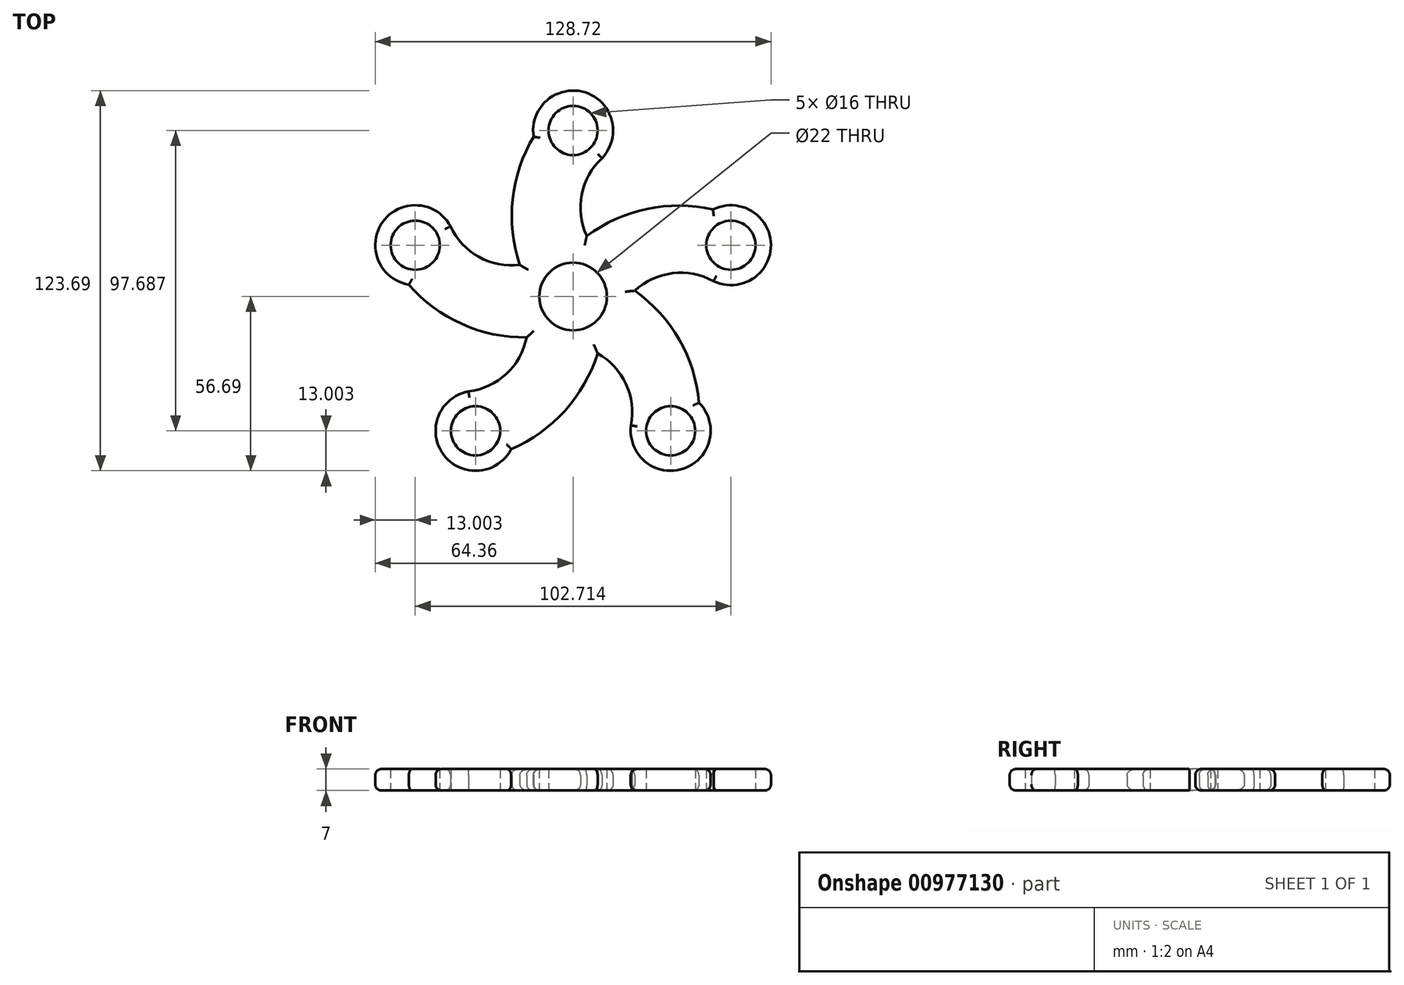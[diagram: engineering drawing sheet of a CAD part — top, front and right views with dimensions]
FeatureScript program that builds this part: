
annotation { "Feature Type Name" : "Feature", "Feature Type Description" : "" }
export const myFeature = defineFeature(function(context is Context, id is Id, definition is map)
    precondition{}
    {
        {
            var Q0;
            Q0=qCreatedBy(makeId("Top.planeOp"),FACE);
            var sketch = newSketch(context, id + "F0", { "sketchPlane" : qUnion([Q0])});
            skCircle(sketch, "E0", {"center": v(0, 0) * mm, "radius": 11 * mm});
            skCircle(sketch, "E1", {"center": v(0, 0) * mm, "radius": 16 * mm});
            skCircle(sketch, "E2", {"center": v(0, 54) * mm, "radius": 8 * mm});
            skCircle(sketch, "E3", {"center": v(0, 54) * mm, "radius": 13 * mm});
            skArc(sketch, "E4", {"start": v(9.38, 45) * mm, "mid": v(2.44, 27.47) * mm, "end": v(11.62, 11) * mm});
            skArc(sketch, "E5", {"start": v(-12.85, 52) * mm, "mid": v(-19.9, 28.8) * mm, "end": v(-15.2, 5) * mm});
            skSolve(sketch);
        }
        {
            var Q0;
            Q0=makeQuery(id+"F0.imprint","IMPRINT",FACE,{"disambiguationData":[TD([[makeQuery(id+"F0.imprint","IMPRINT",EDGE,{"derivedFrom":sQuery(id+"F0.wireOp",EDGE,"E0")}),-1.0]])]});
            var Q1;
            {var subQ0=sQuery(id+"F0.wireOp",EDGE,"E5");Q1=makeQuery(id+"F0.imprint","IMPRINT",FACE,{"disambiguationData":[TD([[makeQuery(id+"F0.imprint","IMPRINT",EDGE,{"derivedFrom":subQ0}),1.0]])]});}
            var Q2;
            Q2=makeQuery(id+"F0.imprint","IMPRINT",FACE,{"disambiguationData":[TD([[makeQuery(id+"F0.imprint","IMPRINT",EDGE,{"derivedFrom":sQuery(id+"F0.wireOp",EDGE,"E2")}),-1.0]])]});
            extrude(context, id + "F1", {"entities" : qUnion([Q0, Q1, Q2]), "depth" : 7 * mm, "offsetDistance" : 25 * mm});
        }
        {
            var Q0;
            Q0=makeQuery(id+"F1.opExtrude","SWEPT_BODY",BODY,{"disambiguationData":[OSD([sQuery(id+"F0.wireOp",EDGE,"E0"),sQuery(id+"F0.wireOp",EDGE,"E1"),sQuery(id+"F0.wireOp",EDGE,"E2"),sQuery(id+"F0.wireOp",EDGE,"E3"),sQuery(id+"F0.wireOp",EDGE,"E4"),sQuery(id+"F0.wireOp",EDGE,"E5")])]});
            var Q1;
            Q1=sQuery(id+"F0.wireOp",EDGE,"E0");
            circularPattern(context, id + "F2", {"operationType" : NewBodyOperationType.ADD, "entities" : qUnion([Q0]), "axis" : qUnion([Q1]), "angle" : 360 * degree, "instanceCount" : 5, "equalSpace" : true});
        }
        {
            var Q0;
            Q0=makeQuery(id+"F2.opPattern","COPY",EDGE,{"derivedFrom":makeQuery(id+"F1.opExtrude","CAP_EDGE",EDGE,{"disambiguationData":[OSD([sQuery(id+"F0.wireOp",EDGE,"E4")])],"isStart":true}),"instanceName":"3"});
            var Q1;
            Q1=makeQuery(id+"F2.opPattern","COPY",EDGE,{"derivedFrom":makeQuery(id+"F1.opExtrude","CAP_EDGE",EDGE,{"disambiguationData":[OSD([sQuery(id+"F0.wireOp",EDGE,"E3")])],"isStart":true}),"instanceName":"3"});
            var Q2;
            Q2=makeQuery(id+"F2.opPattern","COPY",EDGE,{"derivedFrom":makeQuery(id+"F1.opExtrude","CAP_EDGE",EDGE,{"disambiguationData":[OSD([sQuery(id+"F0.wireOp",EDGE,"E4")])],"isStart":false}),"instanceName":"3"});
            var Q3;
            Q3=makeQuery(id+"F2.opPattern","COPY",EDGE,{"derivedFrom":makeQuery(id+"F1.opExtrude","CAP_EDGE",EDGE,{"disambiguationData":[OSD([sQuery(id+"F0.wireOp",EDGE,"E3")])],"isStart":false}),"instanceName":"3"});
            var Q4;
            Q4=makeQuery(id+"F2.opPattern","COPY",EDGE,{"derivedFrom":makeQuery(id+"F1.opExtrude","CAP_EDGE",EDGE,{"disambiguationData":[OSD([sQuery(id+"F0.wireOp",EDGE,"E5")])],"isStart":true}),"instanceName":"2"});
            var Q5;
            Q5=makeQuery(id+"F2.opPattern","COPY",EDGE,{"derivedFrom":makeQuery(id+"F1.opExtrude","CAP_EDGE",EDGE,{"disambiguationData":[OSD([sQuery(id+"F0.wireOp",EDGE,"E5")])],"isStart":false}),"instanceName":"2"});
            var Q6;
            Q6=makeQuery(id+"F2.opPattern","COPY",EDGE,{"derivedFrom":makeQuery(id+"F1.opExtrude","CAP_EDGE",EDGE,{"disambiguationData":[OSD([sQuery(id+"F0.wireOp",EDGE,"E3")])],"isStart":true}),"instanceName":"2"});
            var Q7;
            Q7=makeQuery(id+"F2.opPattern","COPY",EDGE,{"derivedFrom":makeQuery(id+"F1.opExtrude","CAP_EDGE",EDGE,{"disambiguationData":[OSD([sQuery(id+"F0.wireOp",EDGE,"E4")])],"isStart":true}),"instanceName":"2"});
            var Q8;
            Q8=makeQuery(id+"F2.opPattern","COPY",EDGE,{"derivedFrom":makeQuery(id+"F1.opExtrude","CAP_EDGE",EDGE,{"disambiguationData":[OSD([sQuery(id+"F0.wireOp",EDGE,"E5")])],"isStart":false}),"instanceName":"3"});
            var Q9;
            Q9=makeQuery(id+"F2.opPattern","COPY",EDGE,{"derivedFrom":makeQuery(id+"F1.opExtrude","CAP_EDGE",EDGE,{"disambiguationData":[OSD([sQuery(id+"F0.wireOp",EDGE,"E5")])],"isStart":true}),"instanceName":"3"});
            var Q10;
            Q10=makeQuery(id+"F2.opPattern","COPY",EDGE,{"derivedFrom":makeQuery(id+"F1.opExtrude","CAP_EDGE",EDGE,{"disambiguationData":[OSD([sQuery(id+"F0.wireOp",EDGE,"E4")])],"isStart":true}),"instanceName":"4"});
            var Q11;
            Q11=makeQuery(id+"F2.opPattern","COPY",EDGE,{"derivedFrom":makeQuery(id+"F1.opExtrude","CAP_EDGE",EDGE,{"disambiguationData":[OSD([sQuery(id+"F0.wireOp",EDGE,"E4")])],"isStart":false}),"instanceName":"4"});
            var Q12;
            Q12=makeQuery(id+"F2.opPattern","COPY",EDGE,{"derivedFrom":makeQuery(id+"F1.opExtrude","CAP_EDGE",EDGE,{"disambiguationData":[OSD([sQuery(id+"F0.wireOp",EDGE,"E3")])],"isStart":true}),"instanceName":"4"});
            var Q13;
            Q13=makeQuery(id+"F2.opPattern","COPY",EDGE,{"derivedFrom":makeQuery(id+"F1.opExtrude","CAP_EDGE",EDGE,{"disambiguationData":[OSD([sQuery(id+"F0.wireOp",EDGE,"E3")])],"isStart":false}),"instanceName":"4"});
            var Q14;
            Q14=makeQuery(id+"F2.opPattern","COPY",EDGE,{"derivedFrom":makeQuery(id+"F1.opExtrude","CAP_EDGE",EDGE,{"disambiguationData":[OSD([sQuery(id+"F0.wireOp",EDGE,"E5")])],"isStart":true}),"instanceName":"4"});
            var Q15;
            Q15=makeQuery(id+"F2.opPattern","COPY",EDGE,{"derivedFrom":makeQuery(id+"F1.opExtrude","CAP_EDGE",EDGE,{"disambiguationData":[OSD([sQuery(id+"F0.wireOp",EDGE,"E5")])],"isStart":false}),"instanceName":"4"});
            var Q16;
            Q16=makeQuery(id+"F1.opExtrude","CAP_EDGE",EDGE,{"disambiguationData":[OSD([sQuery(id+"F0.wireOp",EDGE,"E4")])],"isStart":true});
            var Q17;
            Q17=makeQuery(id+"F1.opExtrude","CAP_EDGE",EDGE,{"disambiguationData":[OSD([sQuery(id+"F0.wireOp",EDGE,"E4")])],"isStart":false});
            var Q18;
            Q18=makeQuery(id+"F1.opExtrude","CAP_EDGE",EDGE,{"disambiguationData":[OSD([sQuery(id+"F0.wireOp",EDGE,"E5")])],"isStart":false});
            var Q19;
            Q19=makeQuery(id+"F2.opPattern","COPY",EDGE,{"derivedFrom":makeQuery(id+"F1.opExtrude","CAP_EDGE",EDGE,{"disambiguationData":[OSD([sQuery(id+"F0.wireOp",EDGE,"E4")])],"isStart":true}),"instanceName":"1"});
            var Q20;
            Q20=makeQuery(id+"F2.opPattern","COPY",EDGE,{"derivedFrom":makeQuery(id+"F1.opExtrude","CAP_EDGE",EDGE,{"disambiguationData":[OSD([sQuery(id+"F0.wireOp",EDGE,"E4")])],"isStart":false}),"instanceName":"1"});
            var Q21;
            Q21=makeQuery(id+"F2.opPattern","COPY",EDGE,{"derivedFrom":makeQuery(id+"F1.opExtrude","CAP_EDGE",EDGE,{"disambiguationData":[OSD([sQuery(id+"F0.wireOp",EDGE,"E3")])],"isStart":true}),"instanceName":"1"});
            var Q22;
            Q22=makeQuery(id+"F2.opPattern","COPY",EDGE,{"derivedFrom":makeQuery(id+"F1.opExtrude","CAP_EDGE",EDGE,{"disambiguationData":[OSD([sQuery(id+"F0.wireOp",EDGE,"E3")])],"isStart":false}),"instanceName":"1"});
            var Q23;
            Q23=makeQuery(id+"F2.opPattern","COPY",EDGE,{"derivedFrom":makeQuery(id+"F1.opExtrude","CAP_EDGE",EDGE,{"disambiguationData":[OSD([sQuery(id+"F0.wireOp",EDGE,"E5")])],"isStart":true}),"instanceName":"1"});
            var Q24;
            Q24=makeQuery(id+"F2.opPattern","COPY",EDGE,{"derivedFrom":makeQuery(id+"F1.opExtrude","CAP_EDGE",EDGE,{"disambiguationData":[OSD([sQuery(id+"F0.wireOp",EDGE,"E5")])],"isStart":false}),"instanceName":"1"});
            var Q25;
            Q25=makeQuery(id+"F2.opPattern","COPY",EDGE,{"derivedFrom":makeQuery(id+"F1.opExtrude","CAP_EDGE",EDGE,{"disambiguationData":[OSD([sQuery(id+"F0.wireOp",EDGE,"E3")])],"isStart":false}),"instanceName":"2"});
            var Q26;
            Q26=makeQuery(id+"F1.opExtrude","CAP_EDGE",EDGE,{"disambiguationData":[OSD([sQuery(id+"F0.wireOp",EDGE,"E5")])],"isStart":true});
            var Q27;
            Q27=makeQuery(id+"F1.opExtrude","CAP_EDGE",EDGE,{"disambiguationData":[OSD([sQuery(id+"F0.wireOp",EDGE,"E3")])],"isStart":false});
            var Q28;
            Q28=makeQuery(id+"F1.opExtrude","CAP_EDGE",EDGE,{"disambiguationData":[OSD([sQuery(id+"F0.wireOp",EDGE,"E3")])],"isStart":true});
            var Q29;
            Q29=makeQuery(id+"F2.opPattern","COPY",EDGE,{"derivedFrom":makeQuery(id+"F1.opExtrude","CAP_EDGE",EDGE,{"disambiguationData":[OSD([sQuery(id+"F0.wireOp",EDGE,"E4")])],"isStart":false}),"instanceName":"2"});
            fillet(context, id + "F3", {"entities" : qUnion([Q0, Q1, Q2, Q3, Q4, Q5, Q6, Q7, Q8, Q9, Q10, Q11, Q12, Q13, Q14, Q15, Q16, Q17, Q18, Q19, Q20, Q21, Q22, Q23, Q24, Q25, Q26, Q27, Q28, Q29]), "radius" : 2 * mm, "tangentPropagation" : true, "allowEdgeOverflow" : false});
        }
    });
